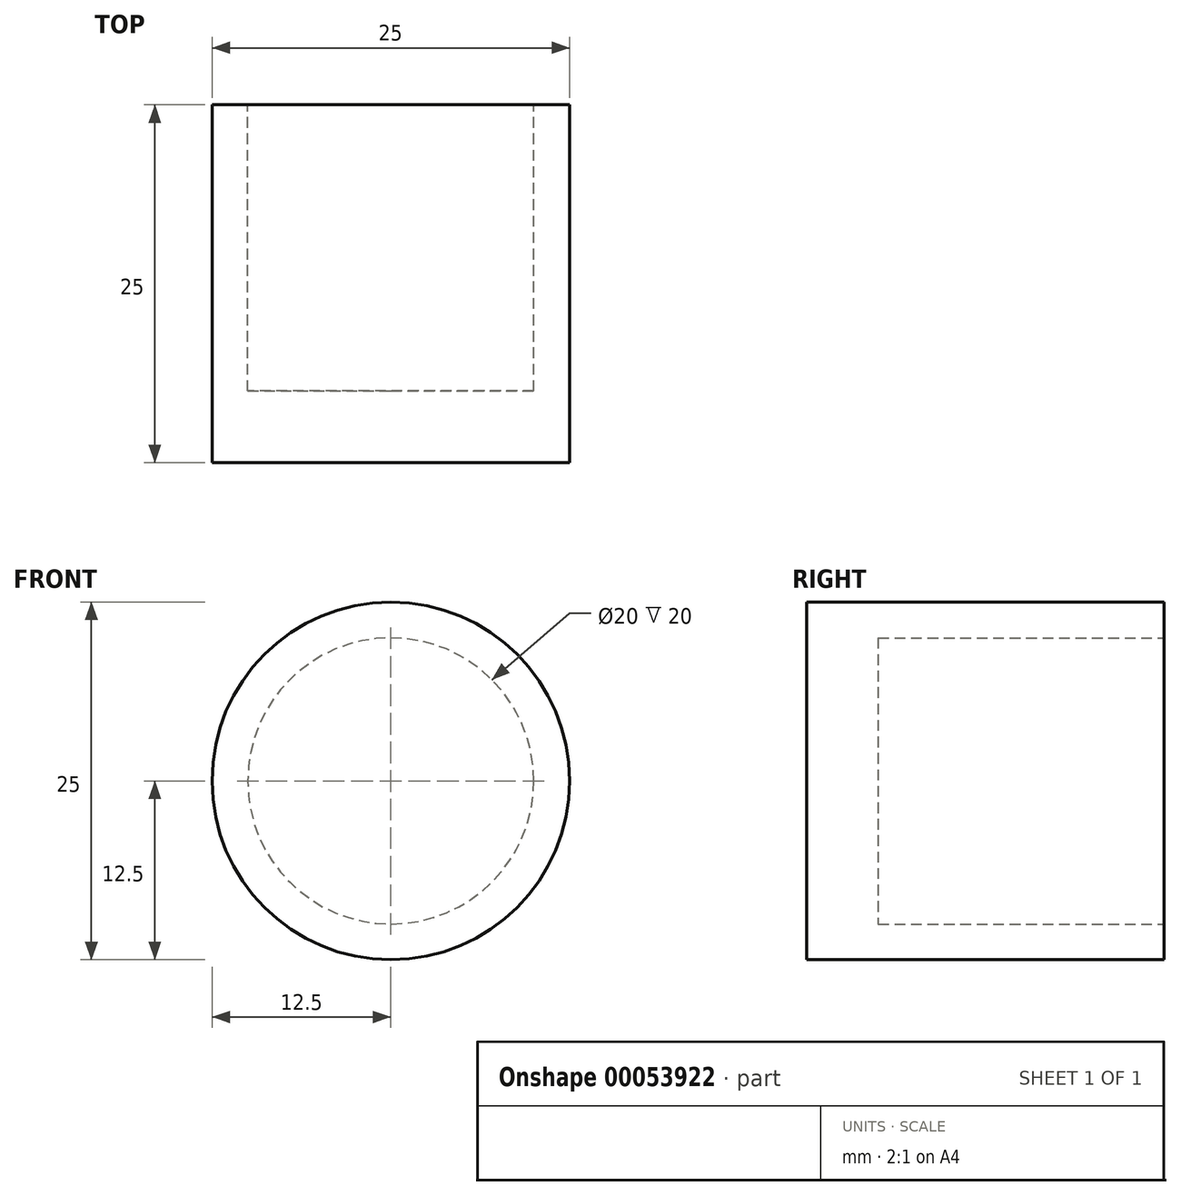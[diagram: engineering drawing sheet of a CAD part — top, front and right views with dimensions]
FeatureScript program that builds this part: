
annotation { "Feature Type Name" : "Feature", "Feature Type Description" : "" }
export const myFeature = defineFeature(function(context is Context, id is Id, definition is map)
    precondition{}
    {
        {
            var Q0;
            Q0=qCreatedBy(makeId("Front.planeOp"),FACE);
            var sketch = newSketch(context, id + "F0", { "sketchPlane" : qUnion([Q0])});
            skCircle(sketch, "E0", {"center": v(0, 0) * mm, "radius": 12.5 * mm});
            skSolve(sketch);
        }
        {
            var Q0;
            Q0 = qSketchRegion(id + "F0", true);
            extrude(context, id + "F1", {"entities" : qUnion([Q0]), "depth" : 25 * mm});
        }
        {
            var Q0;
            Q0=makeQuery(id+"F1.opExtrude","CAP_FACE",FACE,{"disambiguationData":[OSD([sQuery(id+"F0.wireOp",EDGE,"E0")])],"isStart":true});
            var sketch = newSketch(context, id + "F2", { "sketchPlane" : qUnion([Q0])});
            skCircle(sketch, "E1", {"center": v(0, 0) * mm, "radius": 10 * mm});
            skSolve(sketch);
        }
        {
            var Q0;
            Q0 = qSketchRegion(id + "F2", true);
            extrude(context, id + "F3", {"entities" : qUnion([Q0]), "operationType" : NewBodyOperationType.REMOVE, "oppositeDirection" : true, "depth" : 20 * mm});
        }
    });
